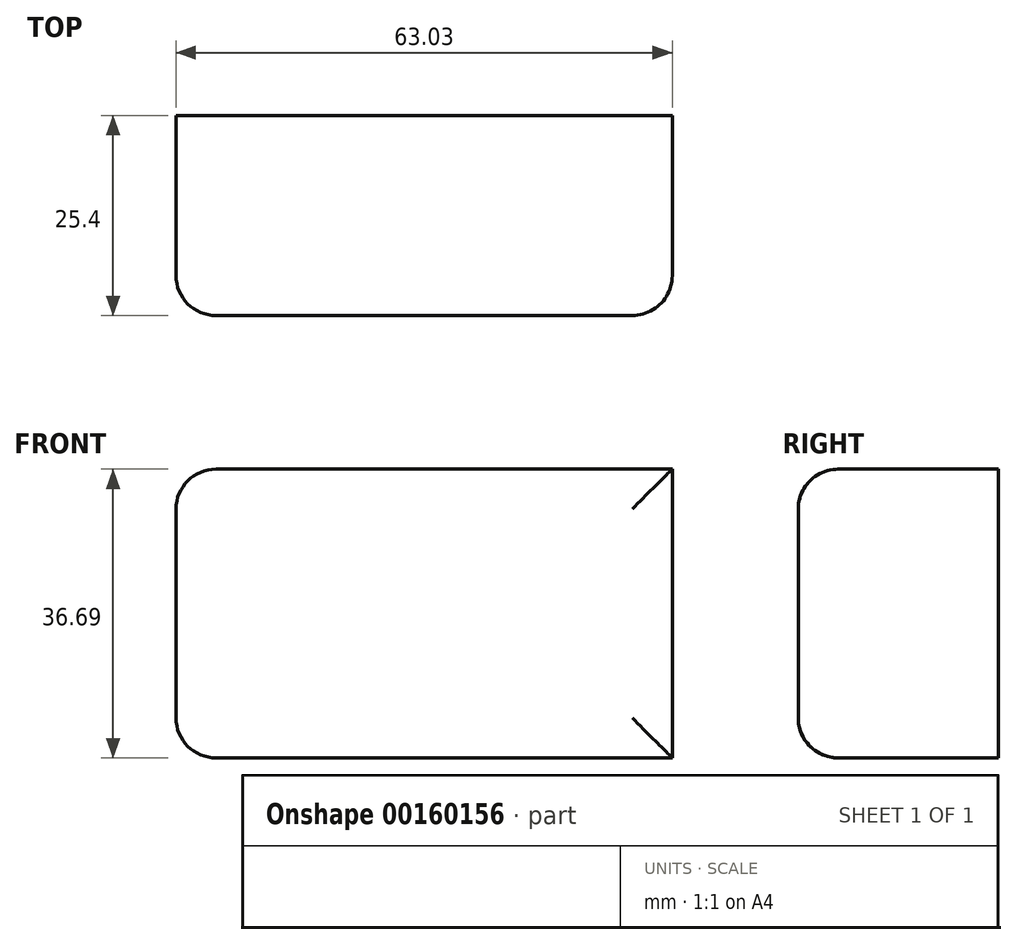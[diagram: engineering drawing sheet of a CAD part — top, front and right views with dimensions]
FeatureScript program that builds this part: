
annotation { "Feature Type Name" : "Feature", "Feature Type Description" : "" }
export const myFeature = defineFeature(function(context is Context, id is Id, definition is map)
    precondition{}
    {
        {
            var Q0;
            Q0=qCreatedBy(makeId("Front.planeOp"),FACE);
            var sketch = newSketch(context, id + "F0", { "sketchPlane" : qUnion([Q0])});
            skLineSegment(sketch, "E0.bottom", {"start": v(-34.05, 20.3) * mm, "end": v(28.98, 20.3) * mm});
            skLineSegment(sketch, "E0.top", {"start": v(-34.05, -16.4) * mm, "end": v(28.98, -16.4) * mm});
            skLineSegment(sketch, "E0.left", {"start": v(-34.05, 20.3) * mm, "end": v(-34.05, -16.4) * mm});
            skLineSegment(sketch, "E0.right", {"start": v(28.98, 20.3) * mm, "end": v(28.98, -16.4) * mm});
            skSolve(sketch);
        }
        {
            var Q0;
            Q0 = qSketchRegion(id + "F0", true);
            extrude(context, id + "F1", {"entities" : qUnion([Q0]), "depth" : 25.4 * mm});
        }
        {
            var Q0;
            Q0=makeQuery(id+"F1.opExtrude","CAP_EDGE",EDGE,{"disambiguationData":[OSD([sQuery(id+"F0.wireOp",EDGE,"E0.left")])],"isStart":false});
            fillet(context, id + "F2", {"entities" : qUnion([Q0]), "radius" : 5.08 * mm, "tangentPropagation" : true, "allowEdgeOverflow" : false});
        }
        {
            var Q0;
            Q0=makeQuery(id+"F1.opExtrude","CAP_EDGE",EDGE,{"disambiguationData":[OSD([sQuery(id+"F0.wireOp",EDGE,"E0.top")])],"isStart":false});
            var Q1;
            Q1=makeQuery(id+"F1.opExtrude","CAP_EDGE",EDGE,{"disambiguationData":[OSD([sQuery(id+"F0.wireOp",EDGE,"E0.right")])],"isStart":false});
            var Q2;
            Q2=makeQuery(id+"F1.opExtrude","CAP_EDGE",EDGE,{"disambiguationData":[OSD([sQuery(id+"F0.wireOp",EDGE,"E0.bottom")])],"isStart":false});
            fillet(context, id + "F3", {"entities" : qUnion([Q0, Q1, Q2]), "radius" : 5.08 * mm, "tangentPropagation" : true, "allowEdgeOverflow" : false});
        }
    });
